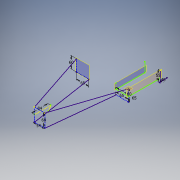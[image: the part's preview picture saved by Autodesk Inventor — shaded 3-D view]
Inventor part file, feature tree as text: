
AUTODESK INVENTOR PART (.ipt)
format: ipt  version: 2018 (Build 220112000, 112)  size: 129,536 bytes
history: native  units: in
note: dims shown in document units (in); Inventor stores cm internally (conversion verified against a paired STEP export)
features: other x7, reference x4, sketch x2
ambient origin geometry x8: Origin, YZ Plane, XZ Plane, XY Plane, X Axis, Y Axis, Z Axis, Center Point
feature tree (13):
  sketch  "Sketch1"  dims[d1=6.8898in d3=0.2492in d4=0.376in d5=0.2756in d6=1.063in d7=1.063in d8=0.25in d9=1.063in d12=2.6772in d13=2.126in d14=2.3622in d15=2.5591in d16=2.3622in d17=2.5591in d18=2.5591in d21=2.1654in d22=0.1575in d23=1.5748in d24=3.3071in]
  sketch  "3D Sketch1"
  other  "Forward Spar-Bulkhead Plane"
  other  "Floor Plane"
  other  "Outboard Wing Brace Plane"
  other  "Inboard Wing Brace Plane"
  reference  "Reference3"
  reference  "Reference4"
  reference  "Reference5"
  reference  "Reference6"
  other  "Aircraft Preliminary Design and W+B.iam"
  other  "Main Landing Gear:2"
  other  "Main Landing Gear:1"
